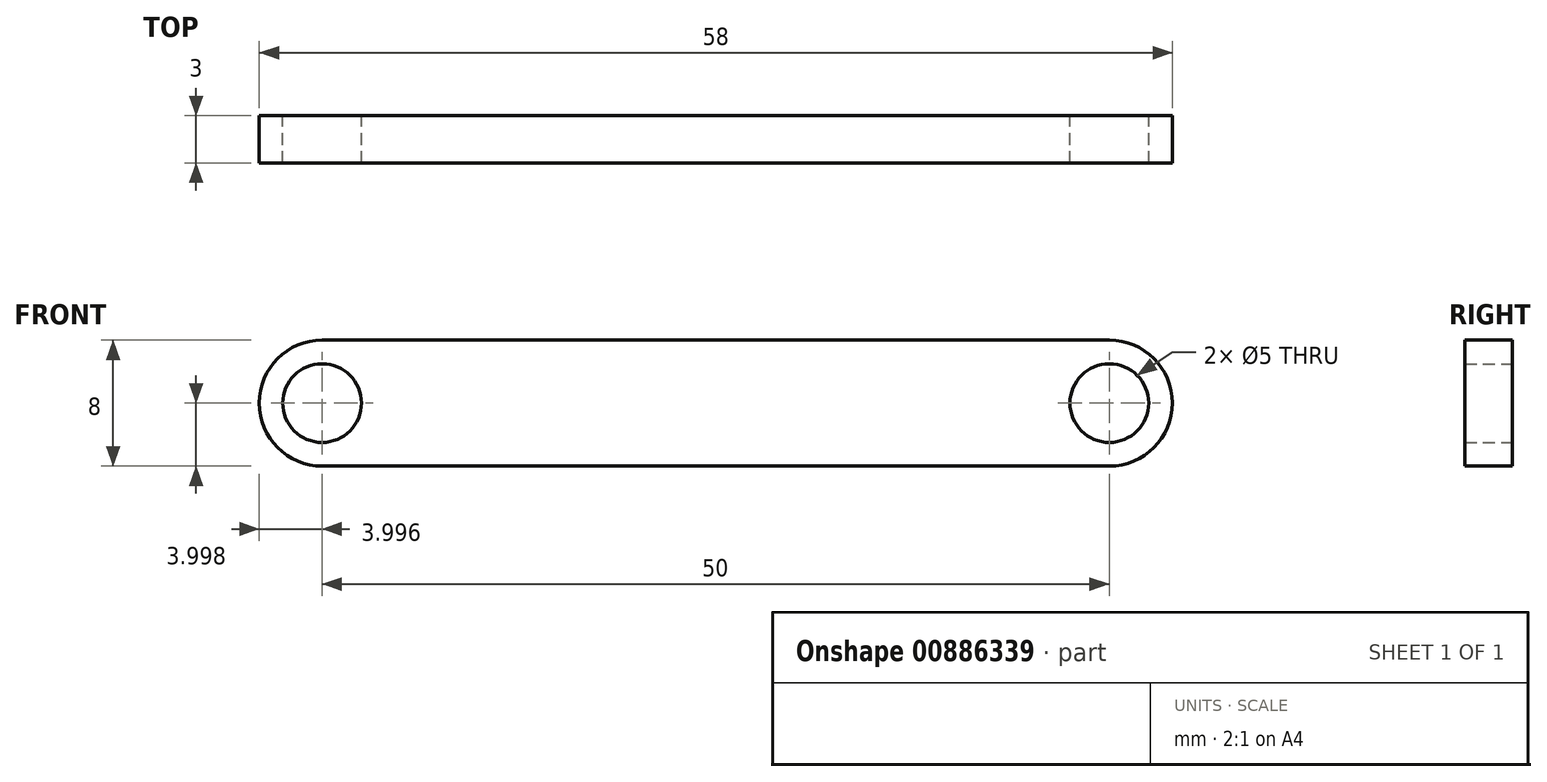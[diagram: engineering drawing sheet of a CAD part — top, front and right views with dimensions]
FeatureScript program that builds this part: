
annotation { "Feature Type Name" : "Feature", "Feature Type Description" : "" }
export const myFeature = defineFeature(function(context is Context, id is Id, definition is map)
    precondition{}
    {
        {
            var Q0;
            Q0=qCreatedBy(makeId("Front.planeOp"),FACE);
            var sketch = newSketch(context, id + "F0", { "sketchPlane" : qUnion([Q0])});
            skLineSegment(sketch, "E0.bottom", {"start": v(-25.17, 21.2) * mm, "end": v(24.83, 21.2) * mm});
            skLineSegment(sketch, "E0.top", {"start": v(-25.17, 13.2) * mm, "end": v(24.83, 13.2) * mm});
            skArc(sketch, "E1", {"start": v(-25.17, 21.2) * mm, "mid": v(-29.17, 17.2) * mm, "end": v(-25.17, 13.2) * mm});
            skArc(sketch, "E2", {"start": v(24.83, 13.2) * mm, "mid": v(28.83, 17.2) * mm, "end": v(24.83, 21.2) * mm});
            skCircle(sketch, "E3", {"center": v(-25.17, 17.2) * mm, "radius": 2.5 * mm});
            skCircle(sketch, "E4", {"center": v(24.83, 17.2) * mm, "radius": 2.5 * mm});
            skSolve(sketch);
        }
        {
            var Q0;
            Q0=makeQuery(id+"F0.imprint","IMPRINT",FACE,{"disambiguationData":[TD([[makeQuery(id+"F0.imprint","IMPRINT",EDGE,{"derivedFrom":sQuery(id+"F0.wireOp",EDGE,"E0.bottom")}),-1.0]])]});
            extrude(context, id + "F1", {"entities" : qUnion([Q0]), "depth" : 3 * mm, "offsetDistance" : 25 * mm});
        }
    });
